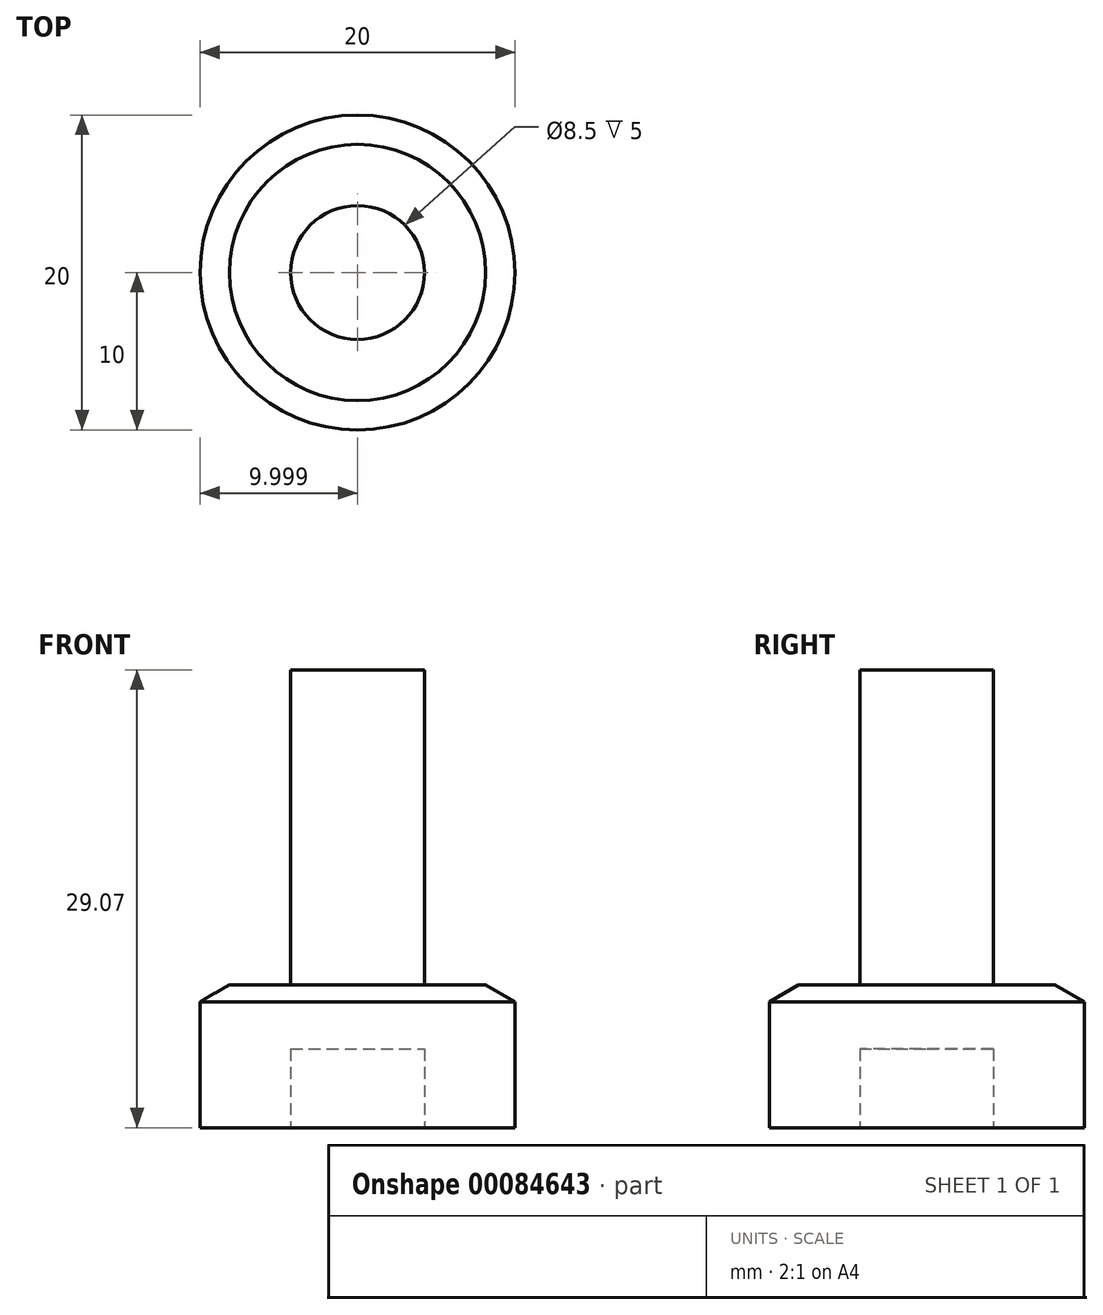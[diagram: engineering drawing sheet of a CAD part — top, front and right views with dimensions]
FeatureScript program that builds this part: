
annotation { "Feature Type Name" : "Feature", "Feature Type Description" : "" }
export const myFeature = defineFeature(function(context is Context, id is Id, definition is map)
    precondition{}
    {
        {
            var Q0;
            Q0=qCreatedBy(makeId("Front.planeOp"),FACE);
            var sketch = newSketch(context, id + "F0", { "sketchPlane" : qUnion([Q0])});
            skLineSegment(sketch, "E0.bottom", {"start": v(-30.55, 8) * mm, "end": v(-20.55, 8) * mm});
            skLineSegment(sketch, "E0.top", {"start": v(-30.55, 0) * mm, "end": v(-24.8, 0) * mm});
            skLineSegment(sketch, "E0.left", {"start": v(-30.55, 8) * mm, "end": v(-30.55, 0) * mm});
            skPoint(sketch, "E1", {"position": v(-20.55, 8) * mm});
            skPoint(sketch, "E2", {"position": v(-20.55, 0) * mm});
            skPoint(sketch, "E3", {"position": v(-20.55, 9.07) * mm});
            skLineSegment(sketch, "E4", {"start": v(-20.55, 8) * mm, "end": v(-20.55, 9.07) * mm});
            skLineSegment(sketch, "E5", {"start": v(-30.55, 8) * mm, "end": v(-28.7, 9.07) * mm});
            skLineSegment(sketch, "E6", {"start": v(-28.7, 9.07) * mm, "end": v(-20.55, 9.07) * mm});
            skLineSegment(sketch, "E7", {"start": v(-20.55, 8) * mm, "end": v(-20.55, 5) * mm});
            skPoint(sketch, "E0.right.end.orphan", {"position": v(-10.55, 0) * mm});
            skPoint(sketch, "E8.start.orphan", {"position": v(-10.55, 8) * mm});
            skLineSegment(sketch, "E9", {"start": v(-20.55, 9.07) * mm, "end": v(-20.55, 29.07) * mm});
            skLineSegment(sketch, "E10", {"start": v(-20.55, 29.07) * mm, "end": v(-24.8, 29.07) * mm});
            skLineSegment(sketch, "E11", {"start": v(-24.8, 29.07) * mm, "end": v(-24.8, 0) * mm});
            skPoint(sketch, "E12.start.orphan", {"position": v(-20.55, 4) * mm});
            skLineSegment(sketch, "E13", {"start": v(-20.55, 5) * mm, "end": v(-24.8, 5) * mm});
            skPoint(sketch, "E14", {"position": v(-20.55, 5) * mm});
            skSolve(sketch);
        }
        {
            var Q0;
            {var subQ0=sQuery(id+"F0.wireOp",EDGE,"E9");Q0=makeQuery(id+"F0.imprint","IMPRINT",FACE,{"disambiguationData":[TD([[makeQuery(id+"F0.imprint","IMPRINT",EDGE,{"derivedFrom":subQ0}),1.0]])]});}
            var Q1;
            {var subQ5=sQuery(id+"F0.wireOp",EDGE,"E0.top");Q1=makeQuery(id+"F0.imprint","IMPRINT",FACE,{"disambiguationData":[TD([[makeQuery(id+"F0.imprint","IMPRINT",EDGE,{"derivedFrom":subQ5}),1.0]])]});}
            var Q2;
            {var subQ0=sQuery(id+"F0.wireOp",EDGE,"E5");Q2=makeQuery(id+"F0.imprint","IMPRINT",FACE,{"disambiguationData":[TD([[makeQuery(id+"F0.imprint","IMPRINT",EDGE,{"derivedFrom":subQ0}),-1.0]])]});}
            var Q3;
            {var subQ0=sQuery(id+"F0.wireOp",EDGE,"E7");Q3=makeQuery(id+"F0.imprint","IMPRINT",FACE,{"disambiguationData":[TD([[makeQuery(id+"F0.imprint","IMPRINT",EDGE,{"derivedFrom":subQ0}),-1.0]])]});}
            var Q4;
            {var subQ0=sQuery(id+"F0.wireOp",EDGE,"E4");Q4=makeQuery(id+"F0.imprint","IMPRINT",FACE,{"disambiguationData":[TD([[makeQuery(id+"F0.imprint","IMPRINT",EDGE,{"derivedFrom":subQ0}),1.0]])]});}
            var Q5;
            Q5=sQuery(id+"F0.wireOp",EDGE,"E9");
            revolve(context, id + "F1", {"entities" : qUnion([Q0, Q1, Q2, Q3, Q4]), "axis" : qUnion([Q5]), "revolveType" : RevolveType.FULL});
        }
    });
